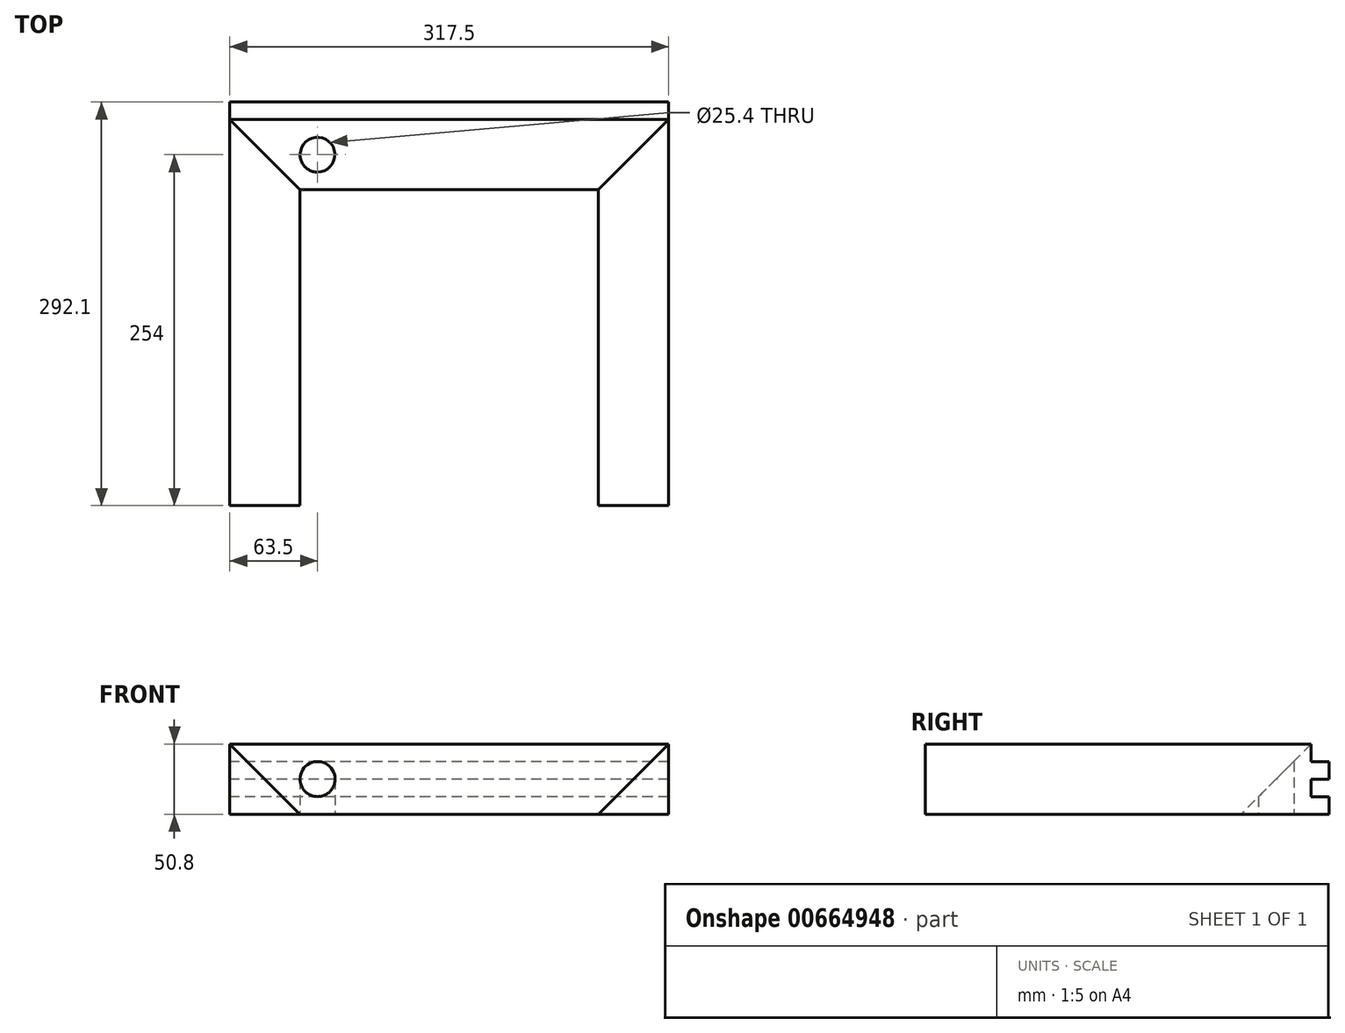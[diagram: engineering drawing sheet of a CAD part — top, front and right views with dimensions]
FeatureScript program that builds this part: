
annotation { "Feature Type Name" : "Feature", "Feature Type Description" : "" }
export const myFeature = defineFeature(function(context is Context, id is Id, definition is map)
    precondition{}
    {
        {
            var Q0;
            Q0=qCreatedBy(makeId("Top.planeOp"),FACE);
            var sketch = newSketch(context, id + "F0", { "sketchPlane" : qUnion([Q0])});
            skLineSegment(sketch, "E0.bottom", {"start": v(0, 0) * mm, "end": v(317.5, 0) * mm});
            skLineSegment(sketch, "E0.top", {"start": v(0, 50.8) * mm, "end": v(317.5, 50.8) * mm});
            skLineSegment(sketch, "E0.left", {"start": v(0, 0) * mm, "end": v(0, 50.8) * mm});
            skLineSegment(sketch, "E0.right", {"start": v(317.5, 0) * mm, "end": v(317.5, 50.8) * mm});
            skLineSegment(sketch, "E1.bottom", {"start": v(0, 0) * mm, "end": v(50.8, 0) * mm});
            skLineSegment(sketch, "E1.top", {"start": v(0, -228.6) * mm, "end": v(50.8, -228.6) * mm});
            skLineSegment(sketch, "E1.left", {"start": v(0, 0) * mm, "end": v(0, -228.6) * mm});
            skLineSegment(sketch, "E1.right", {"start": v(50.8, 0) * mm, "end": v(50.8, -228.6) * mm});
            skLineSegment(sketch, "E2.bottom", {"start": v(317.5, 0) * mm, "end": v(266.7, 0) * mm});
            skLineSegment(sketch, "E2.top", {"start": v(317.5, -228.6) * mm, "end": v(266.7, -228.6) * mm});
            skLineSegment(sketch, "E2.left", {"start": v(317.5, 0) * mm, "end": v(317.5, -228.6) * mm});
            skLineSegment(sketch, "E2.right", {"start": v(266.7, 0) * mm, "end": v(266.7, -228.6) * mm});
            skSolve(sketch);
        }
        {
            var Q0;
            Q0=makeQuery(id+"F0.imprint","IMPRINT",FACE,{"disambiguationData":[TD([[makeQuery(id+"F0.imprint","IMPRINT",EDGE,{"derivedFrom":sQuery(id+"F0.wireOp",EDGE,"E1.top")}),1.0]])]});
            var Q1;
            Q1=makeQuery(id+"F0.imprint","IMPRINT",FACE,{"disambiguationData":[TD([[makeQuery(id+"F0.imprint","IMPRINT",EDGE,{"derivedFrom":sQuery(id+"F0.wireOp",EDGE,"E0.top")}),-1.0]])]});
            var Q2;
            Q2=makeQuery(id+"F0.imprint","IMPRINT",FACE,{"disambiguationData":[TD([[makeQuery(id+"F0.imprint","IMPRINT",EDGE,{"derivedFrom":sQuery(id+"F0.wireOp",EDGE,"E2.top")}),-1.0]])]});
            extrude(context, id + "F1", {"entities" : qUnion([Q0, Q1, Q2]), "depth" : 50.8 * mm, "offsetDistance" : 25.4 * mm});
        }
        {
            var Q0;
            Q0=makeQuery(id+"F1.opExtrude","CAP_EDGE",EDGE,{"disambiguationData":[OSD([sQuery(id+"F0.wireOp",EDGE,"E1.right")])],"isStart":false});
            var Q1;
            Q1=makeQuery(id+"F1.opExtrude","CAP_EDGE",EDGE,{"disambiguationData":[OSD([sQuery(id+"F0.wireOp",EDGE,"E0.bottom")])],"isStart":false});
            var Q2;
            Q2=makeQuery(id+"F1.opExtrude","CAP_EDGE",EDGE,{"disambiguationData":[OSD([sQuery(id+"F0.wireOp",EDGE,"E2.right")])],"isStart":false});
            chamfer(context, id + "F2", {"entities" : qUnion([Q0, Q1, Q2]), "width" : 50.8 * mm, "tangentPropagation" : true});
        }
        {
            var Q0;
            Q0=makeQuery(id+"F1.opExtrude","SWEPT_FACE",FACE,{"disambiguationData":[OSD([sQuery(id+"F0.wireOp",EDGE,"E0.top")])]});
            var sketch = newSketch(context, id + "F3", { "sketchPlane" : qUnion([Q0])});
            skLineSegment(sketch, "E3.bottom", {"start": v(-317.5, 50.8) * mm, "end": v(0, 50.8) * mm});
            skLineSegment(sketch, "E3.top", {"start": v(-317.5, 38.1) * mm, "end": v(0, 38.1) * mm});
            skLineSegment(sketch, "E3.left", {"start": v(-317.5, 50.8) * mm, "end": v(-317.5, 38.1) * mm});
            skLineSegment(sketch, "E3.right", {"start": v(0, 50.8) * mm, "end": v(0, 38.1) * mm});
            skLineSegment(sketch, "E4", {"start": v(-317.5, 38.1) * mm, "end": v(-317.5, 25.4) * mm});
            skLineSegment(sketch, "E5.bottom", {"start": v(-317.5, 25.4) * mm, "end": v(0, 25.4) * mm});
            skLineSegment(sketch, "E5.top", {"start": v(-317.5, 12.7) * mm, "end": v(0, 12.7) * mm});
            skLineSegment(sketch, "E5.left", {"start": v(-317.5, 25.4) * mm, "end": v(-317.5, 12.7) * mm});
            skLineSegment(sketch, "E5.right", {"start": v(0, 25.4) * mm, "end": v(0, 12.7) * mm});
            skLineSegment(sketch, "E6", {"start": v(-317.5, 12.7) * mm, "end": v(-317.5, 0) * mm});
            skLineSegment(sketch, "E7.bottom", {"start": v(-317.5, 0) * mm, "end": v(0, 0) * mm});
            skLineSegment(sketch, "E7.top", {"start": v(-317.5, 0) * mm, "end": v(0, 0) * mm});
            skLineSegment(sketch, "E7.left", {"start": v(-317.5, 0) * mm, "end": v(-317.5, 0) * mm});
            skLineSegment(sketch, "E7.right", {"start": v(0, 0) * mm, "end": v(0, 0) * mm});
            skSolve(sketch);
        }
        {
            var Q0;
            Q0=makeQuery(id+"F1.opExtrude","CAP_FACE",FACE,{"disambiguationData":[OSD([sQuery(id+"F0.wireOp",EDGE,"E0.bottom"),sQuery(id+"F0.wireOp",EDGE,"E0.top"),sQuery(id+"F0.wireOp",EDGE,"E0.left"),sQuery(id+"F0.wireOp",EDGE,"E0.right"),sQuery(id+"F0.wireOp",EDGE,"E1.top"),sQuery(id+"F0.wireOp",EDGE,"E1.left"),sQuery(id+"F0.wireOp",EDGE,"E1.right"),sQuery(id+"F0.wireOp",EDGE,"E2.top"),sQuery(id+"F0.wireOp",EDGE,"E2.left"),sQuery(id+"F0.wireOp",EDGE,"E2.right")])],"isStart":true});
            var sketch = newSketch(context, id + "F4", { "sketchPlane" : qUnion([Q0])});
            skCircle(sketch, "E8", {"center": v(63.5, -25.4) * mm, "radius": 12.7 * mm});
            skSolve(sketch);
        }
        {
            var Q0;
            Q0=makeQuery(id+"F4.imprint","IMPRINT",FACE,{"disambiguationData":[TD([[makeQuery(id+"F4.imprint","IMPRINT",EDGE,{"derivedFrom":sQuery(id+"F4.wireOp",EDGE,"E8")}),1.0]])]});
            extrude(context, id + "F5", {"entities" : qUnion([Q0]), "operationType" : NewBodyOperationType.REMOVE, "oppositeDirection" : true, "depth" : 63.5 * mm, "offsetDistance" : 25.4 * mm});
        }
        {
            var Q0;
            {var subQ0=sQuery(id+"F3.wireOp",EDGE,"E5.top");Q0=makeQuery(id+"F3.imprint","IMPRINT",FACE,{"disambiguationData":[TD([[makeQuery(id+"F3.imprint","IMPRINT",EDGE,{"derivedFrom":subQ0}),-1.0]])]});}
            var Q1;
            {var subQ0=sQuery(id+"F3.wireOp",EDGE,"E3.top");Q1=makeQuery(id+"F3.imprint","IMPRINT",FACE,{"disambiguationData":[TD([[makeQuery(id+"F3.imprint","IMPRINT",EDGE,{"derivedFrom":subQ0}),-1.0]])]});}
            extrude(context, id + "F6", {"entities" : qUnion([Q0, Q1]), "operationType" : NewBodyOperationType.ADD, "depth" : 12.7 * mm, "offsetDistance" : 25.4 * mm});
        }
    });
